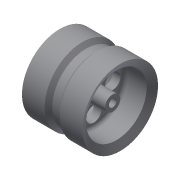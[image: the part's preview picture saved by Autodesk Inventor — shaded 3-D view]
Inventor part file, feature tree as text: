
AUTODESK INVENTOR PART (.ipt)
format: ipt  version: 2015 (Build 190159000, 159)  size: 186,880 bytes
history: native  units: mm
features: sketch x6, hole x3, revolve x1
ambient origin geometry x8: Origin, YZ Plane, XZ Plane, XY Plane, X Axis, Y Axis, Z Axis, Center Point
bodies: Solid1 (feature_tree)
feature tree (10):
  revolve  "Revolution1"  [1 undecoded]
  hole  "Hole1"  [1 undecoded]
  hole  "Hole2"  [1 undecoded]
  sketch  "Sketch4"  dims[d14=90.0deg d15=3.0mm]
  hole  "Hole3"  [1 undecoded]
  sketch  "Sketch6"  dims[d17=3.0mm d18=3.0mm d19=5.0mm d20=6.0mm d21=4.0mm d22=2.0mm d23=90.0deg d24=8.0mm d25=0.0mm d26=5.0mm d27=5.0mm d28=6.0mm d29=5.0mm d30=5.0mm d31=3.0mm d32=3.0mm d33=3.0mm d34=3.0mm d35=4.0mm d36=6.0mm d37=4.0mm d38=2.0mm d39=90.0deg d40=8.0mm d41=0.0mm d42=2.0mm d43=6.0mm d44=4.0mm d45=2.0mm d46=90.0deg d47=20.0mm d48=0.0mm d49=2.0mm d50=2.0mm d51=1.0mm]
  sketch  "Sketch1"  dims[d0=6.0mm d1=2.0mm]
  sketch  "Sketch2"  dims[d3=5.0mm d6=12.0mm]
  sketch  "Sketch3"  dims[d7=2.0mm d8=5.0mm]
  sketch  "Sketch5"  dims[d16=3.0mm]
note: 4 required parameter values undecoded (feature->parameter linkage not recoverable at this tier; creation-order binding heuristic only, values carry confidence <= 0.55)